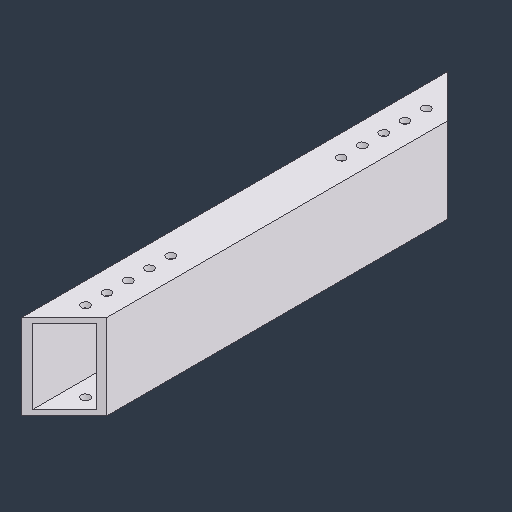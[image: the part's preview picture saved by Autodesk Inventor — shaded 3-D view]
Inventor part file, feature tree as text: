
AUTODESK INVENTOR PART (.ipt)
format: ipt  version: 2024.3 (Build 283343000, 343)  size: 156,672 bytes
history: native  units: in
note: dims shown in document units (in); Inventor stores cm internally (conversion verified against a paired STEP export)
features: sketch x3, extrude x2, hole x1, mirror x1, projected_geometry x1
ambient origin geometry x8: Origin, YZ Plane, XZ Plane, XY Plane, X Axis, Y Axis, Z Axis, Center Point
bodies: Solid1 (feature_tree)
feature tree (8):
  extrude  "Extrusion1"  Depth=2.0in
  extrude  "Extrusion2"  Depth=0.125in TaperAngle=0.0deg
  hole  "Hole1"  [1 undecoded]
  mirror  "Mirror1"
  sketch  "Sketch1"  dims[d0=1.0in d1=2.0in]
  sketch  "Sketch2"  dims[d2=0.125in d3=10.0in d4=0.0in]
  projected_geometry  "Projected Loop1"
  sketch  "Sketch4"  dims[d6=45.0deg d7=0.0in d8=0.0in d9=0.5in d10=1.0in d11=1.9685in d13=0.5in d14=0.3937in d16=1.0in d18=0.201in d19=0.38in d20=0.375in d21=0.25in d22=0.5635in d23=1.0in d24=0.8108in]
note: 1 required parameter value undecoded (feature->parameter linkage not recoverable at this tier; creation-order binding heuristic only, values carry confidence <= 0.55)
